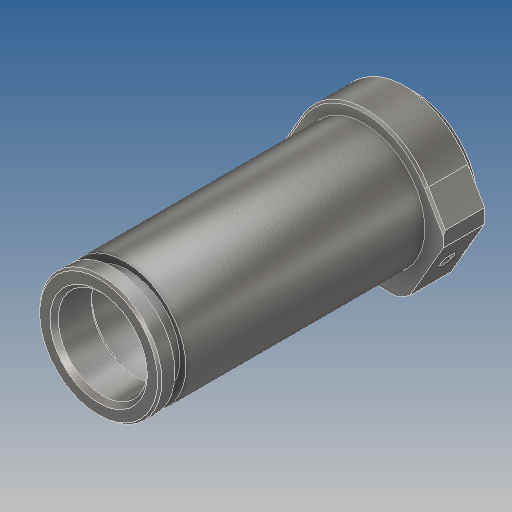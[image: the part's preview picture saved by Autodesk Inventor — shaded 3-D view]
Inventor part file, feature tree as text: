
AUTODESK INVENTOR PART (.ipt)
format: ipt  version: 2019 (Build 230136000, 136)  size: 303,104 bytes
history: native  units: mm
features: chamfer x5, sketch x3, other x2, extrude x1, hole x1, pattern_circular x1, projected_geometry x1
ambient origin geometry x8: Origin, YZ Plane, XZ Plane, XY Plane, X Axis, Y Axis, Z Axis, Center Point
bodies: Solide1 (feature_tree)
feature tree (14):
  other  "Révolution1"
  other  "Plan de construction1"
  extrude  "Extrusion1"  Depth=29.5mm
  chamfer  "Chanfrein1"  Distance=8.0mm
  chamfer  "Chanfrein2"  Distance=4.0mm
  hole  "Perçage1"  [1 undecoded]
  chamfer  "Chanfrein3"  Distance=2.0mm
  pattern_circular  "Réseau circulaire1"  [2 undecoded]
  chamfer  "Chanfrein4"  Angle=90.0deg  [1 undecoded]
  chamfer  "Chanfrein5"  [1 undecoded]
  sketch  "Esquisse1"
  sketch  "Esquisse3"
  sketch  "Esquisse4"
  projected_geometry  "Boucle projetée1"
note: 5 required parameter values undecoded (feature->parameter linkage not recoverable at this tier; creation-order binding heuristic only, values carry confidence <= 0.55)
